# Revit family: Spannschlossmutter nach DIN 1479 M10
name_source: partatom
category: HLS-Bauteile
revit_build: Autodesk Revit 2017 (Build: 20190507_1515(x64)
units: mm (PartAtom-declared; Revit-internal decimal feet)

## family parameters
Arbeitsebenenbasiert = Nein
Beim Laden mit Abzugskörper schneiden = Nein
Bemaßung runder Anschluss = Durchmesser verwenden
Gemeinsam genutzt = Ja
Immer vertikal = Nein
Raumberechnungspunkt = Nein
Teiletyp = Normal

## types (1)
- Spannschlossmutter DIN 1479 M10
    Artikelnummer = 08120760
    EAN = 4250928459268
    F2 = 9 mm
    Fabrikat = MEFA
    Firma = MEFA Befestigungs- und Montagesysteme GmbH
    Gewicht = 0.06 kg
    Gewicht pro Bauteil = 0.06 kg
    Gewinde = M10
    H = 45 mm  [stored 0.147638 ft]
    Innengewinde 1 = M10
    Kurztext1 = Spannschlossmutter
    Kurztext2 = M10 SW 17
    Lochung = 5 mm  [stored 0.0164042 ft]
    Länge = 45 mm  [stored 0.147638 ft]
    Länge Innengewinde 1 = 45 mm
    Material = Stahl
    Mengeneinheit = St
    Oberflaeche = galvanisch verzinkt
    Schlüsselweite = 17
    vpe = 10

note: [stored X ft] marks values corroborated as IEEE doubles in the binary element streams (Revit-internal decimal feet)

## geometry (parser evidence)
native form markers: Sweep x3
no freeform markers — native parametric forms only
